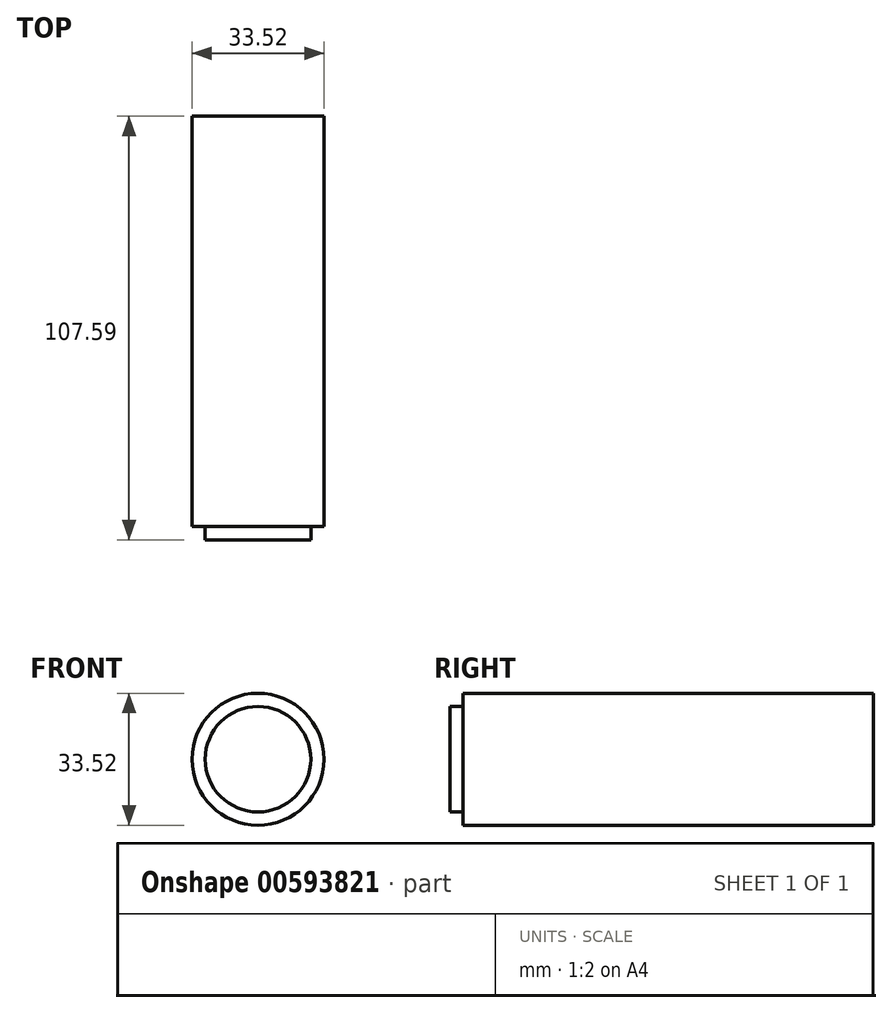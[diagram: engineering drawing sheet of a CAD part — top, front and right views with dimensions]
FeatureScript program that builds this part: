
annotation { "Feature Type Name" : "Feature", "Feature Type Description" : "" }
export const myFeature = defineFeature(function(context is Context, id is Id, definition is map)
    precondition{}
    {
        {
            var Q0;
            Q0=qCreatedBy(makeId("Right.planeOp"),FACE);
            var sketch = newSketch(context, id + "F0", { "sketchPlane" : qUnion([Q0])});
            skLineSegment(sketch, "E0", {"start": v(-55.93, 0) * mm, "end": v(-55.93, 13.41) * mm});
            skLineSegment(sketch, "E1", {"start": v(-55.93, 13.41) * mm, "end": v(-52.58, 13.41) * mm});
            skLineSegment(sketch, "E2", {"start": v(-52.58, 13.41) * mm, "end": v(-52.58, 16.76) * mm});
            skLineSegment(sketch, "E3", {"start": v(-52.58, 16.76) * mm, "end": v(51.66, 16.76) * mm});
            skLineSegment(sketch, "E4", {"start": v(51.66, 16.76) * mm, "end": v(51.66, 0) * mm});
            skLineSegment(sketch, "E5", {"start": v(51.66, 0) * mm, "end": v(-55.93, 0) * mm});
            skSolve(sketch);
        }
        {
            var Q0;
            Q0=makeQuery(id+"F0.imprint","IMPRINT",FACE,{"disambiguationData":[TD([[makeQuery(id+"F0.imprint","IMPRINT",EDGE,{"derivedFrom":sQuery(id+"F0.wireOp",EDGE,"E0")}),-1.0]])]});
            var Q1;
            Q1=sQuery(id+"F0.wireOp",EDGE,"E5");
            revolve(context, id + "F1", {"entities" : qUnion([Q0]), "axis" : qUnion([Q1]), "revolveType" : RevolveType.FULL, "surfaceOperationType" : NewSurfaceOperationType.NEW});
        }
    });
